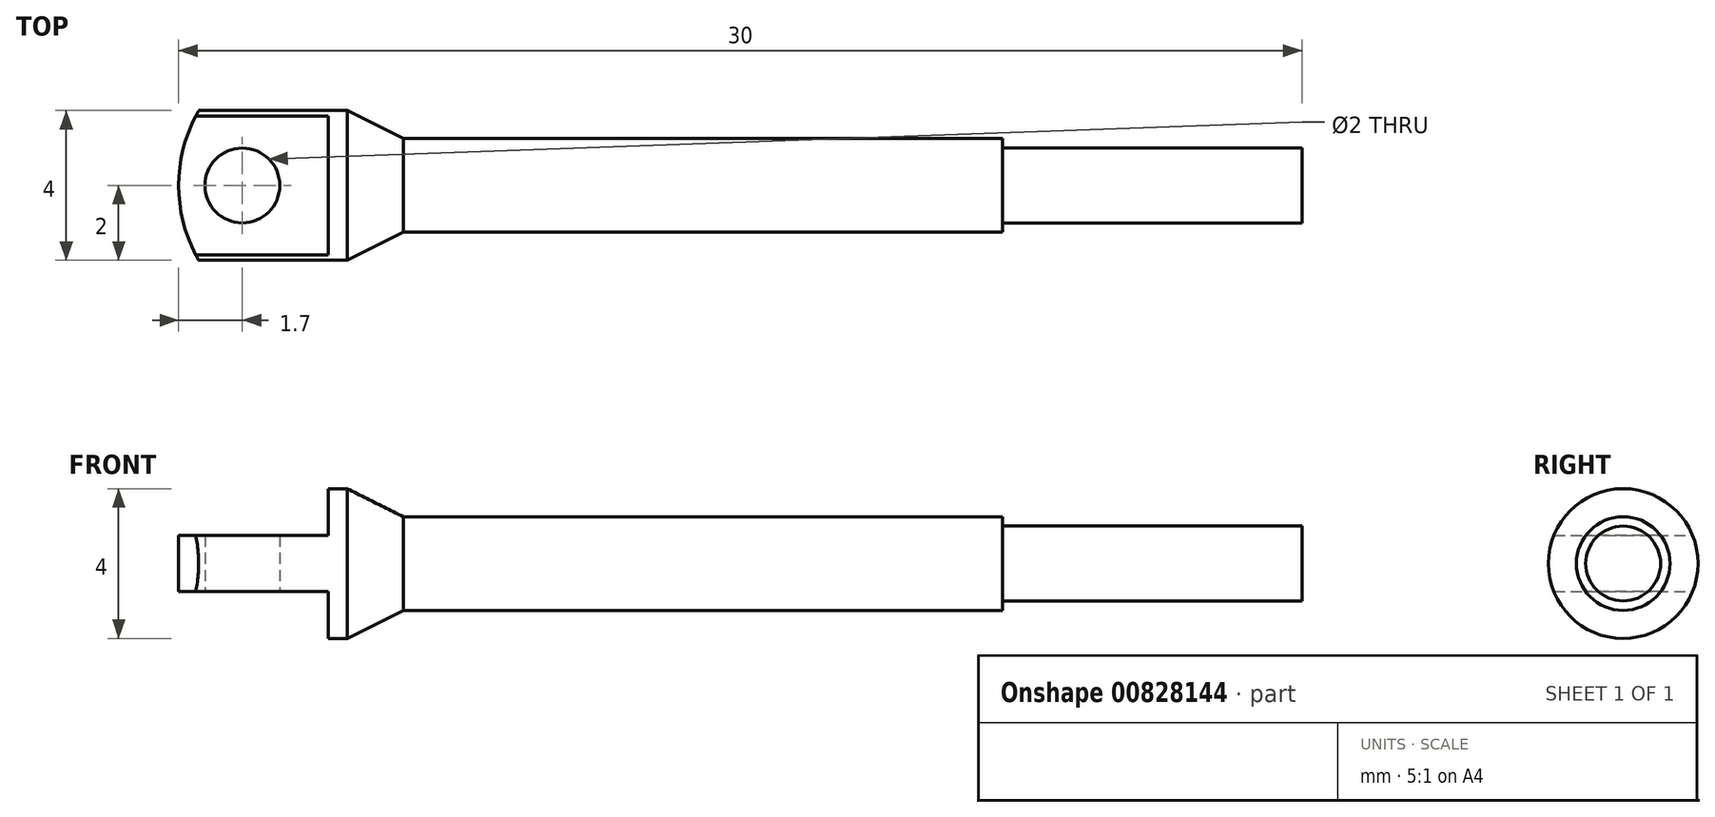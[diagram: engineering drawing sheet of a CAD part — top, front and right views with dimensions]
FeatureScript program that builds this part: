
annotation { "Feature Type Name" : "Feature", "Feature Type Description" : "" }
export const myFeature = defineFeature(function(context is Context, id is Id, definition is map)
    precondition{}
    {
        {
            var Q0;
            Q0=qCreatedBy(makeId("Front.planeOp"),FACE);
            var sketch = newSketch(context, id + "F0", { "sketchPlane" : qUnion([Q0])});
            skLineSegment(sketch, "E0.bottom", {"start": v(0, 0) * mm, "end": v(24, 0) * mm});
            skLineSegment(sketch, "E0.top", {"start": v(0, 1.25) * mm, "end": v(16, 1.25) * mm});
            skLineSegment(sketch, "E0.left", {"start": v(0, 0) * mm, "end": v(0, 1.25) * mm});
            skLineSegment(sketch, "E1", {"start": v(16, 1.25) * mm, "end": v(16, 1) * mm});
            skLineSegment(sketch, "E2", {"start": v(16, 1) * mm, "end": v(24, 1) * mm});
            skLineSegment(sketch, "E3", {"start": v(24, 1) * mm, "end": v(24, 0) * mm});
            skSolve(sketch);
        }
        {
            var Q0;
            Q0 = qSketchRegion(id + "F0", true);
            var Q1;
            Q1=sQuery(id+"F0.wireOp",EDGE,"E0.bottom");
            revolve(context, id + "F1", {"surfaceOperationType" : NewSurfaceOperationType.NEW, "entities" : qUnion([Q0]), "axis" : qUnion([Q1]), "revolveType" : RevolveType.FULL});
        }
        {
            var Q0;
            Q0=qCreatedBy(makeId("Front.planeOp"),FACE);
            var sketch = newSketch(context, id + "F2", { "sketchPlane" : qUnion([Q0])});
            skLineSegment(sketch, "E4", {"start": v(-1.5, 2) * mm, "end": v(0, 1.25) * mm});
            skLineSegment(sketch, "E5", {"start": v(0, 1.25) * mm, "end": v(0, 0) * mm});
            skLineSegment(sketch, "E6", {"start": v(-1.5, 2) * mm, "end": v(-2, 2) * mm});
            skLineSegment(sketch, "E7", {"start": v(-2, 2) * mm, "end": v(-2, 0) * mm});
            skLineSegment(sketch, "E8", {"start": v(-2, 0) * mm, "end": v(0, 0) * mm});
            skSolve(sketch);
        }
        {
            var Q0;
            Q0 = qSketchRegion(id + "F2", true);
            var Q1;
            Q1=sQuery(id+"F2.wireOp",EDGE,"E8");
            revolve(context, id + "F3", {"operationType" : NewBodyOperationType.ADD, "surfaceOperationType" : NewSurfaceOperationType.NEW, "entities" : qUnion([Q0]), "axis" : qUnion([Q1]), "revolveType" : RevolveType.FULL});
        }
        {
            var Q0;
            Q0=qCreatedBy(makeId("Front.planeOp"),FACE);
            var sketch = newSketch(context, id + "F4", { "sketchPlane" : qUnion([Q0])});
            skLineSegment(sketch, "E9.bottom", {"start": v(-2, 0.75) * mm, "end": v(-6, 0.75) * mm});
            skLineSegment(sketch, "E9.top", {"start": v(-2, -0.75) * mm, "end": v(-6, -0.75) * mm});
            skLineSegment(sketch, "E9.left", {"start": v(-2, 0.75) * mm, "end": v(-2, -0.75) * mm});
            skLineSegment(sketch, "E9.right", {"start": v(-6, 0.75) * mm, "end": v(-6, -0.75) * mm});
            skSolve(sketch);
        }
        {
            var Q0;
            Q0 = qSketchRegion(id + "F4", true);
            var Q1;
            Q1=makeQuery(id+"F3.opRevolve","SWEPT_FACE",FACE,{"disambiguationData":[OSD([sQuery(id+"F2.wireOp",EDGE,"E6")])]});
            var Q2;
            Q2=makeQuery(id+"F3.opRevolve","SWEPT_FACE",FACE,{"disambiguationData":[OSD([sQuery(id+"F2.wireOp",EDGE,"E6")])]});
            extrude(context, id + "F5", {"entities" : qUnion([Q0]), "operationType" : NewBodyOperationType.ADD, "endBound" : BoundingType.UP_TO_SURFACE, "depth" : 25 * mm, "endBoundEntityFace" : qUnion([Q1]), "offsetDistance" : 25 * mm, "hasSecondDirection" : true, "secondDirectionBound" : SecondDirectionBoundingType.UP_TO_SURFACE, "secondDirectionOppositeDirection" : true, "secondDirectionDepth" : 25 * mm, "secondDirectionBoundEntityFace" : qUnion([Q2])});
        }
        {
            var Q0;
            Q0=makeQuery(id+"F5.opExtrude","SWEPT_FACE",FACE,{"disambiguationData":[OSD([sQuery(id+"F4.wireOp",EDGE,"E9.top")])]});
            var sketch = newSketch(context, id + "F6", { "sketchPlane" : qUnion([Q0])});
            skCircle(sketch, "E10", {"center": v(-4.3, 0) * mm, "radius": 1 * mm});
            skSolve(sketch);
        }
        {
            var Q0;
            Q0 = qSketchRegion(id + "F6", true);
            extrude(context, id + "F7", {"entities" : qUnion([Q0]), "operationType" : NewBodyOperationType.REMOVE, "endBound" : BoundingType.SYMMETRIC, "oppositeDirection" : true, "depth" : 25 * mm, "offsetDistance" : 25 * mm});
        }
        {
            var Q0;
            Q0=makeQuery(id+"F5.opExtrude","SWEPT_FACE",FACE,{"disambiguationData":[OSD([sQuery(id+"F4.wireOp",EDGE,"E9.top")])]});
            var sketch = newSketch(context, id + "F8", { "sketchPlane" : qUnion([Q0])});
            skArc(sketch, "E11", {"start": v(-5.12, 2.5) * mm, "mid": v(-6, 0) * mm, "end": v(-5.12, -2.5) * mm});
            skLineSegment(sketch, "E12", {"start": v(-5.12, 2.5) * mm, "end": v(-7, 2.5) * mm});
            skLineSegment(sketch, "E13", {"start": v(-7, 2.5) * mm, "end": v(-7, -2.5) * mm});
            skLineSegment(sketch, "E14", {"start": v(-7, -2.5) * mm, "end": v(-5.12, -2.5) * mm});
            skSolve(sketch);
        }
        {
            var Q0;
            Q0 = qSketchRegion(id + "F8", true);
            extrude(context, id + "F9", {"entities" : qUnion([Q0]), "operationType" : NewBodyOperationType.REMOVE, "endBound" : BoundingType.SYMMETRIC, "oppositeDirection" : true, "depth" : 25 * mm, "offsetDistance" : 25 * mm});
        }
    });
